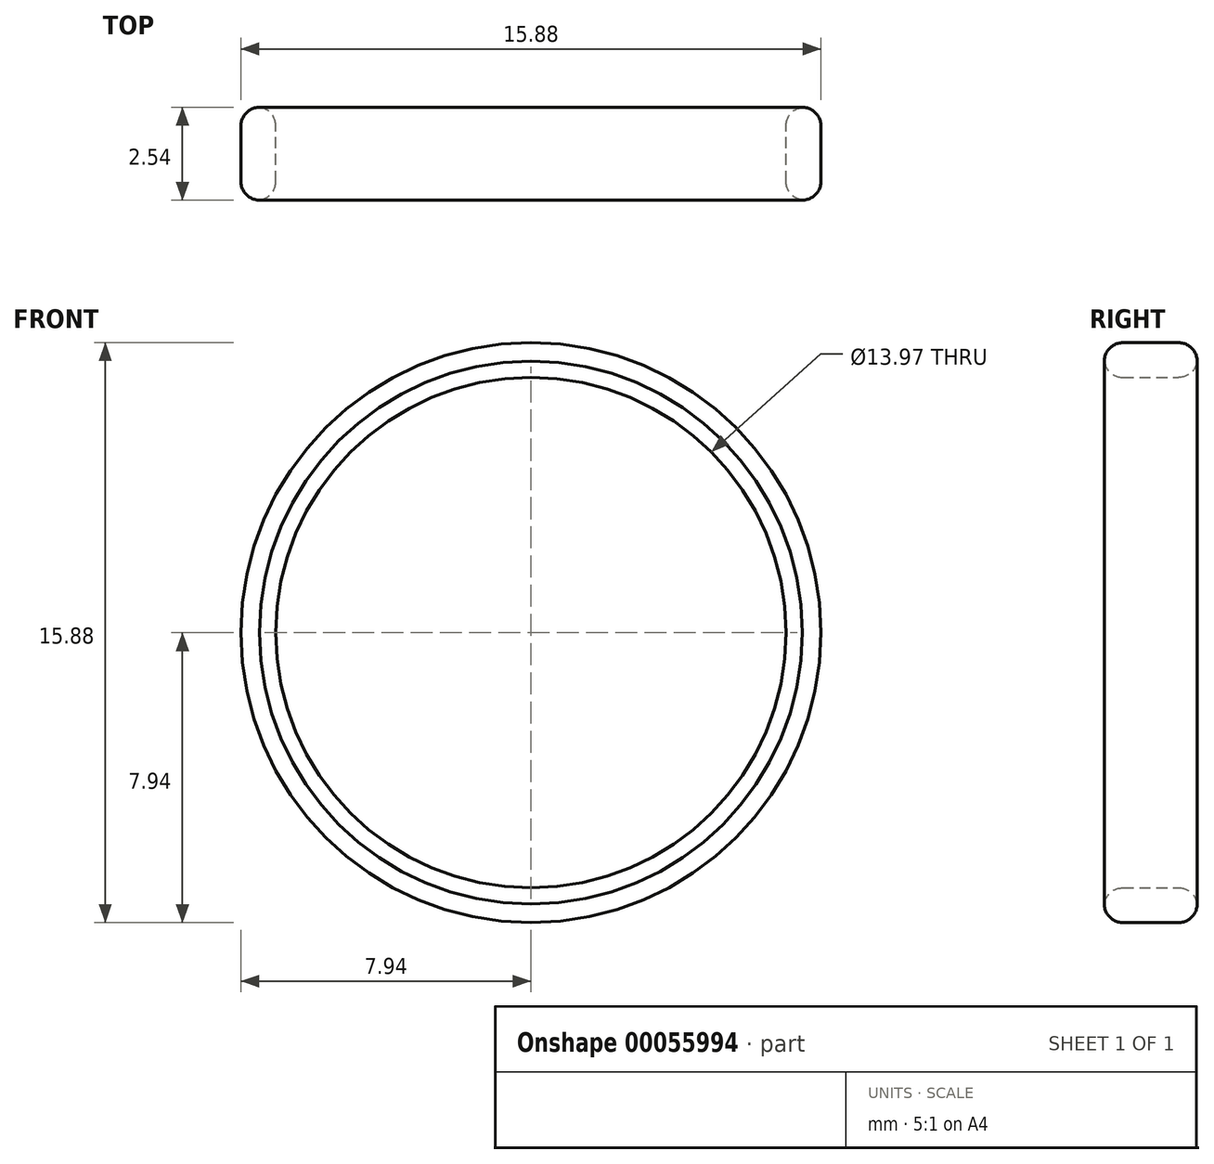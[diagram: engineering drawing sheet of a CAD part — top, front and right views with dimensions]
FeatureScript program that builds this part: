
annotation { "Feature Type Name" : "Feature", "Feature Type Description" : "" }
export const myFeature = defineFeature(function(context is Context, id is Id, definition is map)
    precondition{}
    {
        {
            var Q0;
            Q0=qCreatedBy(makeId("Front.planeOp"),FACE);
            var sketch = newSketch(context, id + "F0", { "sketchPlane" : qUnion([Q0])});
            skCircle(sketch, "E0", {"center": v(0, 0) * mm, "radius": 7.94 * mm});
            skCircle(sketch, "E1", {"center": v(0, 0) * mm, "radius": 6.99 * mm});
            skSolve(sketch);
        }
        {
            var Q0;
            Q0=makeQuery(id+"F0.imprint","IMPRINT",FACE,{"disambiguationData":[TD([[makeQuery(id+"F0.imprint","IMPRINT",EDGE,{"derivedFrom":sQuery(id+"F0.wireOp",EDGE,"E0")}),1.0]])]});
            extrude(context, id + "F1", {"entities" : qUnion([Q0]), "depth" : 2.54 * mm});
        }
        {
            var Q0;
            Q0=makeQuery(id+"F1.opExtrude","CAP_EDGE",EDGE,{"disambiguationData":[OSD([sQuery(id+"F0.wireOp",EDGE,"E0")])],"isStart":false});
            var Q1;
            Q1=makeQuery(id+"F1.opExtrude","CAP_EDGE",EDGE,{"disambiguationData":[OSD([sQuery(id+"F0.wireOp",EDGE,"E0")])],"isStart":true});
            fillet(context, id + "F2", {"entities" : qUnion([Q0, Q1]), "radius" : 0.5 * mm, "tangentPropagation" : true, "allowEdgeOverflow" : false});
        }
        {
            var Q0;
            Q0=makeQuery(id+"F1.opExtrude","CAP_EDGE",EDGE,{"disambiguationData":[OSD([sQuery(id+"F0.wireOp",EDGE,"E1")])],"isStart":true});
            var Q1;
            Q1=makeQuery(id+"F1.opExtrude","CAP_EDGE",EDGE,{"disambiguationData":[OSD([sQuery(id+"F0.wireOp",EDGE,"E1")])],"isStart":false});
            fillet(context, id + "F3", {"entities" : qUnion([Q0, Q1]), "radius" : 0.5 * mm, "tangentPropagation" : true, "allowEdgeOverflow" : false});
        }
    });
